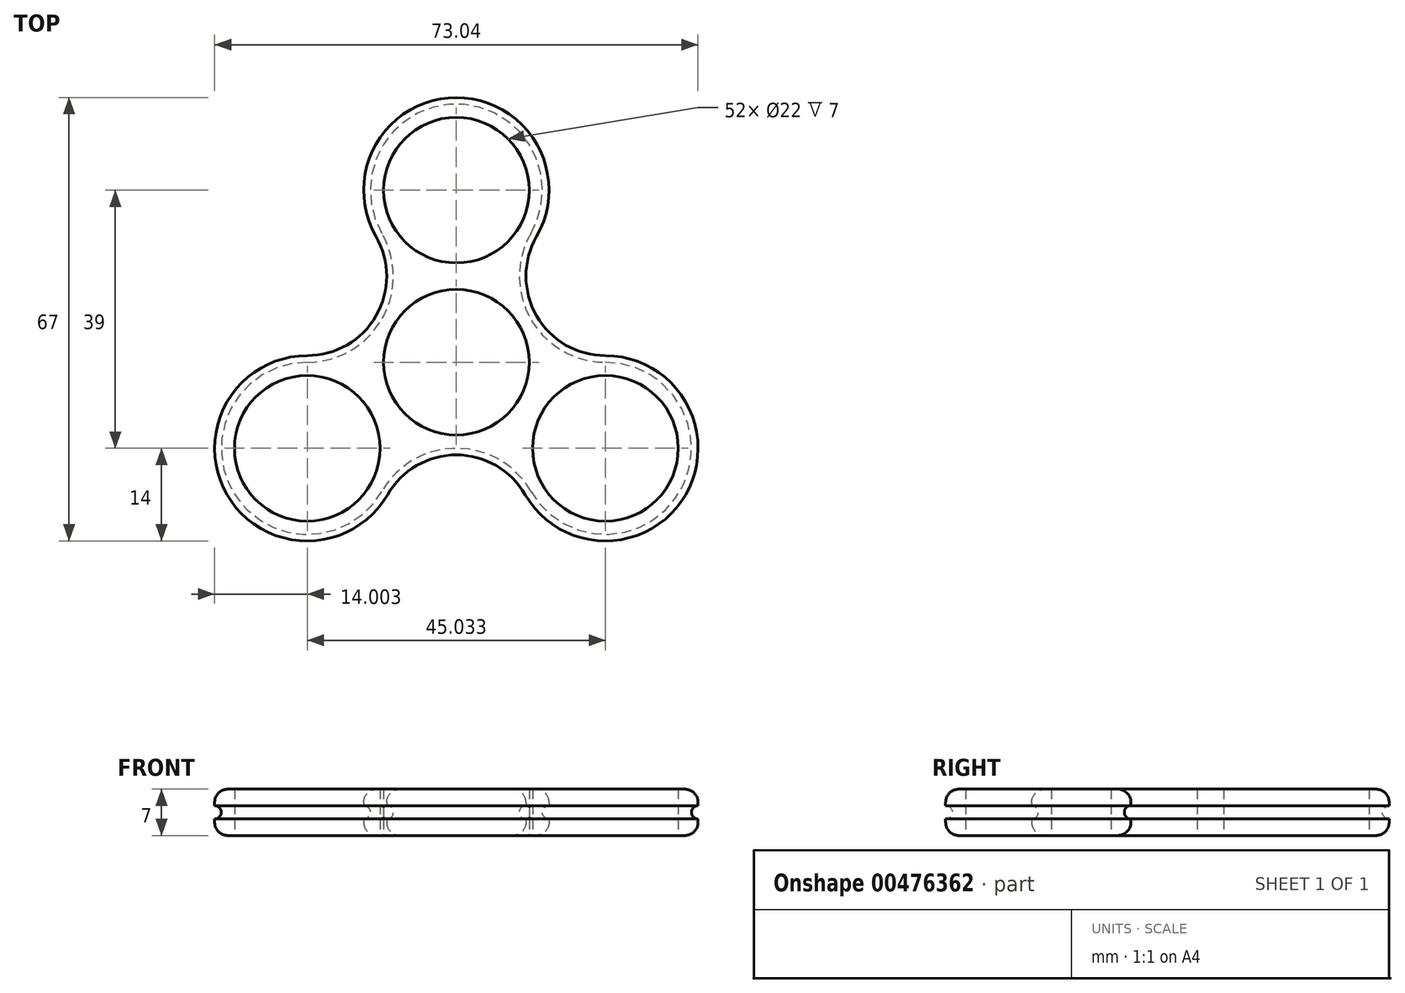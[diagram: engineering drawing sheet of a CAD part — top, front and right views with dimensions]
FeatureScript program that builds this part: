
annotation { "Feature Type Name" : "Feature", "Feature Type Description" : "" }
export const myFeature = defineFeature(function(context is Context, id is Id, definition is map)
    precondition{}
    {
        {
            var Q0;
            Q0=qCreatedBy(makeId("Top.planeOp"),FACE);
            var sketch = newSketch(context, id + "F0", { "sketchPlane" : qUnion([Q0])});
            skCircle(sketch, "E0", {"center": v(0, 0) * mm, "radius": 11 * mm});
            skCircle(sketch, "E1", {"center": v(0, 26) * mm, "radius": 11 * mm});
            skArc(sketch, "E2.0", {"start": v(12.12, 19) * mm, "mid": v(0, 40) * mm, "end": v(-12.12, 19) * mm});
            skCircle(sketch, "E3.1.0", {"center": v(-22.52, -13) * mm, "radius": 11 * mm});
            skArc(sketch, "E3.1.1", {"start": v(-22.52, 1) * mm, "mid": v(-34.64, -20) * mm, "end": v(-10.4, -20) * mm});
            skCircle(sketch, "E3.2.0", {"center": v(22.52, -13) * mm, "radius": 11 * mm});
            skArc(sketch, "E3.2.1", {"start": v(10.4, -20) * mm, "mid": v(34.64, -20) * mm, "end": v(22.52, 1) * mm});
            skArc(sketch, "E4", {"start": v(-12.12, 19) * mm, "mid": v(-12.12, 7) * mm, "end": v(-22.52, 1) * mm});
            skArc(sketch, "E5", {"start": v(12.12, 19) * mm, "mid": v(12.12, 7) * mm, "end": v(22.52, 1) * mm});
            skArc(sketch, "E6", {"start": v(-10.4, -20) * mm, "mid": v(0, -14) * mm, "end": v(10.4, -20) * mm});
            skLineSegment(sketch, "E7", {"start": v(0, 0) * mm, "end": v(12.12, 7) * mm});
            skPoint(sketch, "E8", {"position": v(0, 40) * mm});
            skSolve(sketch);
        }
        {
            var Q0;
            Q0=qCreatedBy(makeId("Right.planeOp"),FACE);
            var sketch = newSketch(context, id + "F1", { "sketchPlane" : qUnion([Q0])});
            skCircle(sketch, "E9", {"center": v(40, 0) * mm, "radius": 1 * mm});
            skSolve(sketch);
        }
        {
            var Q0;
            Q0=makeQuery(id+"F0.imprint","IMPRINT",FACE,{"disambiguationData":[TD([[makeQuery(id+"F0.imprint","IMPRINT",EDGE,{"derivedFrom":sQuery(id+"F0.wireOp",EDGE,"E0")}),-1.0]])]});
            extrude(context, id + "F2", {"entities" : qUnion([Q0]), "endBound" : BoundingType.SYMMETRIC, "depth" : 7 * mm});
        }
        {
            var Q0;
            Q0=qCreatedBy(makeId("Top.planeOp"),FACE);
            var sketch = newSketch(context, id + "F3", { "sketchPlane" : qUnion([Q0])});
            skArc(sketch, "E10.0", {"start": v(0, 40) * mm, "mid": v(-12.12, 33) * mm, "end": v(-12.12, 19) * mm});
            skArc(sketch, "E11.1.0", {"start": v(-22.52, 1) * mm, "mid": v(-34.64, -20) * mm, "end": v(-10.4, -20) * mm});
            skPoint(sketch, "E11.center", {"position": v(0, 0) * mm});
            skArc(sketch, "E12", {"start": v(-12.12, 19) * mm, "mid": v(-12.12, 7) * mm, "end": v(-22.52, 1) * mm});
            skArc(sketch, "E13", {"start": v(0, -14) * mm, "mid": v(-6, -15.6) * mm, "end": v(-10.4, -20) * mm});
            skPoint(sketch, "E14", {"position": v(0, 40) * mm});
            skPoint(sketch, "E15", {"position": v(0, -14) * mm});
            skPoint(sketch, "E16.start.orphan", {"position": v(12.12, 19) * mm});
            skSolve(sketch);
        }
        {
            var Q0;
            Q0=qCreatedBy(makeId("Top.planeOp"),FACE);
            var sketch = newSketch(context, id + "F4", { "sketchPlane" : qUnion([Q0])});
            skArc(sketch, "E17.0", {"start": v(12.12, 19) * mm, "mid": v(12.12, 33) * mm, "end": v(0, 40) * mm});
            skArc(sketch, "E18.2.0", {"start": v(10.4, -20) * mm, "mid": v(34.64, -20) * mm, "end": v(22.52, 1) * mm});
            skPoint(sketch, "E18.center", {"position": v(0, 0) * mm});
            skArc(sketch, "E19", {"start": v(12.12, 19) * mm, "mid": v(12.12, 7) * mm, "end": v(22.52, 1) * mm});
            skArc(sketch, "E20", {"start": v(10.4, -20) * mm, "mid": v(6, -15.6) * mm, "end": v(0, -14) * mm});
            skPoint(sketch, "E21", {"position": v(0, -14) * mm});
            skPoint(sketch, "E22", {"position": v(0, 40) * mm});
            skPoint(sketch, "E23.orphan", {"position": v(-12.12, 19) * mm});
            skSolve(sketch);
        }
        {
            var Q0;
            Q0=makeQuery(id+"F1.imprint","IMPRINT",FACE,{"disambiguationData":[TD([[makeQuery(id+"F1.imprint","IMPRINT",EDGE,{"derivedFrom":sQuery(id+"F1.wireOp",EDGE,"E9")}),1.0]])]});
            var Q1;
            Q1=qConstructionFilter(qBodyType(qCreatedBy(id+"F3",EDGE),BodyType.WIRE),ConstructionObject.NO);
            var Q2;
            Q2=qConstructionFilter(qBodyType(qCreatedBy(id+"F4",EDGE),BodyType.WIRE),ConstructionObject.NO);
            sweep(context, id + "F5", {"operationType" : NewBodyOperationType.REMOVE, "profiles" : qUnion([Q0]), "path" : qUnion([Q1, Q2])});
        }
        {
            var Q0;
            Q0=makeQuery(id+"F2.opExtrude","CAP_EDGE",EDGE,{"disambiguationData":[OSD([sQuery(id+"F0.wireOp",EDGE,"E2.0")])],"isStart":false});
            var Q1;
            Q1=makeQuery(id+"F2.opExtrude","CAP_EDGE",EDGE,{"disambiguationData":[OSD([sQuery(id+"F0.wireOp",EDGE,"E4")])],"isStart":false});
            var Q2;
            Q2=makeQuery(id+"F2.opExtrude","CAP_EDGE",EDGE,{"disambiguationData":[OSD([sQuery(id+"F0.wireOp",EDGE,"E3.1.1")])],"isStart":false});
            var Q3;
            Q3=makeQuery(id+"F2.opExtrude","CAP_EDGE",EDGE,{"disambiguationData":[OSD([sQuery(id+"F0.wireOp",EDGE,"E6")])],"isStart":false});
            var Q4;
            Q4=makeQuery(id+"F2.opExtrude","CAP_EDGE",EDGE,{"disambiguationData":[OSD([sQuery(id+"F0.wireOp",EDGE,"E3.2.1")])],"isStart":false});
            var Q5;
            Q5=makeQuery(id+"F2.opExtrude","CAP_EDGE",EDGE,{"disambiguationData":[OSD([sQuery(id+"F0.wireOp",EDGE,"E5")])],"isStart":false});
            var Q6;
            Q6=makeQuery(id+"F2.opExtrude","CAP_EDGE",EDGE,{"disambiguationData":[OSD([sQuery(id+"F0.wireOp",EDGE,"E3.1.1")])],"isStart":true});
            var Q7;
            Q7=makeQuery(id+"F2.opExtrude","CAP_EDGE",EDGE,{"disambiguationData":[OSD([sQuery(id+"F0.wireOp",EDGE,"E4")])],"isStart":true});
            var Q8;
            Q8=makeQuery(id+"F2.opExtrude","CAP_EDGE",EDGE,{"disambiguationData":[OSD([sQuery(id+"F0.wireOp",EDGE,"E2.0")])],"isStart":true});
            var Q9;
            Q9=makeQuery(id+"F2.opExtrude","CAP_EDGE",EDGE,{"disambiguationData":[OSD([sQuery(id+"F0.wireOp",EDGE,"E5")])],"isStart":true});
            var Q10;
            Q10=makeQuery(id+"F2.opExtrude","CAP_EDGE",EDGE,{"disambiguationData":[OSD([sQuery(id+"F0.wireOp",EDGE,"E3.2.1")])],"isStart":true});
            fillet(context, id + "F6", {"entities" : qUnion([Q0, Q1, Q2, Q3, Q4, Q5, Q6, Q7, Q8, Q9, Q10]), "radius" : 2 * mm, "tangentPropagation" : true, "allowEdgeOverflow" : false});
        }
    });
